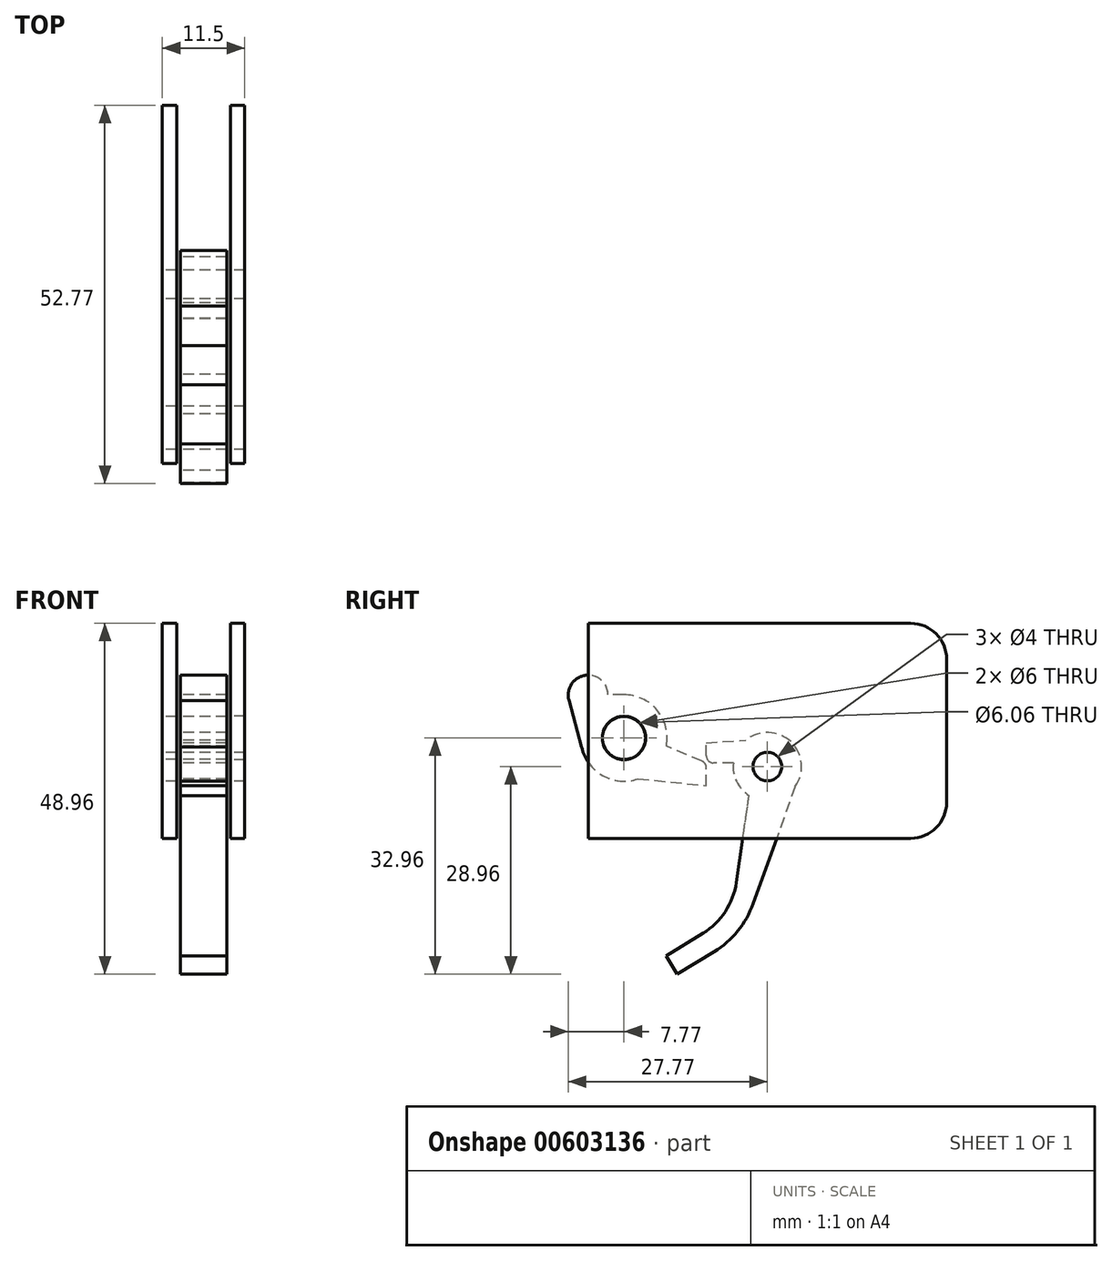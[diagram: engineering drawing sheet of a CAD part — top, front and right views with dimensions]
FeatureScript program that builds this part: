
annotation { "Feature Type Name" : "Feature", "Feature Type Description" : "" }
export const myFeature = defineFeature(function(context is Context, id is Id, definition is map)
    precondition{}
    {
        {
            var Q0;
            Q0=qCreatedBy(makeId("Right.planeOp"),FACE);
            var sketch = newSketch(context, id + "F0", { "sketchPlane" : qUnion([Q0])});
            skLineSegment(sketch, "E0.bottom", {"start": v(-20, 10) * mm, "end": v(25, 10) * mm});
            skLineSegment(sketch, "E0.top", {"start": v(-20, -20) * mm, "end": v(25, -20) * mm});
            skLineSegment(sketch, "E0.left", {"start": v(-20, 10) * mm, "end": v(-20, -20) * mm});
            skLineSegment(sketch, "E0.right", {"start": v(30, 5) * mm, "end": v(30, -15) * mm});
            skCircle(sketch, "E1", {"center": v(-15, -6) * mm, "radius": 3 * mm});
            skCircle(sketch, "E2", {"center": v(5, -10) * mm, "radius": 2 * mm});
            skPoint(sketch, "E3.visualSharp", {"position": v(30, 10) * mm});
            skArc(sketch, "E3.filletArc", {"start": v(30, 5) * mm, "mid": v(28.54, 8.54) * mm, "end": v(25, 10) * mm});
            skPoint(sketch, "E4.visualSharp", {"position": v(30, -20) * mm});
            skArc(sketch, "E4.filletArc", {"start": v(25, -20) * mm, "mid": v(28.54, -18.54) * mm, "end": v(30, -15) * mm});
            skSolve(sketch);
        }
        {
            var Q0;
            Q0 = qSketchRegion(id + "F0", true);
            extrude(context, id + "F1", {"entities" : qUnion([Q0]), "depth" : 2 * mm, "offsetDistance" : 25 * mm});
        }
        {
            var Q0;
            Q0=makeQuery(id+"F1.opExtrude","CAP_FACE",FACE,{"disambiguationData":[OSD([sQuery(id+"F0.wireOp",EDGE,"E0.bottom"),sQuery(id+"F0.wireOp",EDGE,"E0.top"),sQuery(id+"F0.wireOp",EDGE,"E0.left"),sQuery(id+"F0.wireOp",EDGE,"E0.right"),sQuery(id+"F0.wireOp",EDGE,"E1"),sQuery(id+"F0.wireOp",EDGE,"E2"),sQuery(id+"F0.wireOp",EDGE,"E3.filletArc"),sQuery(id+"F0.wireOp",EDGE,"E4.filletArc")])],"isStart":false});
            var sketch = newSketch(context, id + "F2", { "sketchPlane" : qUnion([Q0])});
            skArc(sketch, "E5", {"start": v(-20.9, -7.27) * mm, "mid": v(-17.96, -11.26) * mm, "end": v(-13.03, -11.7) * mm});
            skArc(sketch, "E6", {"start": v(0.25, -9.5) * mm, "mid": v(0.7, -12.08) * mm, "end": v(2.45, -14.04) * mm});
            skArc(sketch, "E7", {"start": v(-17.23, 0.03) * mm, "mid": v(-20.4, 2.74) * mm, "end": v(-22.66, -0.76) * mm});
            skLineSegment(sketch, "E8", {"start": v(-13.03, -11.7) * mm, "end": v(-3.5, -12.66) * mm});
            skLineSegment(sketch, "E9", {"start": v(-3.5, -12.66) * mm, "end": v(-3.5, -10.16) * mm});
            skLineSegment(sketch, "E10", {"start": v(-4.12, -9.24) * mm, "end": v(-9.07, -7.12) * mm});
            skLineSegment(sketch, "E11", {"start": v(0.25, -9.5) * mm, "end": v(-2.5, -9.5) * mm});
            skLineSegment(sketch, "E12", {"start": v(-3.5, -8.5) * mm, "end": v(-3.5, -6.69) * mm});
            skLineSegment(sketch, "E13", {"start": v(-3.5, -6.69) * mm, "end": v(2, -6.28) * mm});
            skPoint(sketch, "E14.visualSharp", {"position": v(-3.5, -9.5) * mm});
            skArc(sketch, "E14.filletArc", {"start": v(-3.5, -8.5) * mm, "mid": v(-3.22, -9.2) * mm, "end": v(-2.5, -9.5) * mm});
            skArc(sketch, "E15.filletArc", {"start": v(-3.5, -10.16) * mm, "mid": v(-3.67, -9.6) * mm, "end": v(-4.12, -9.24) * mm});
            skLineSegment(sketch, "E16", {"start": v(-14.94, 0.03) * mm, "end": v(-17.23, 0.03) * mm});
            skLineSegment(sketch, "E17", {"start": v(8.87, -12.8) * mm, "end": v(3.02, -29.12) * mm});
            skLineSegment(sketch, "E18", {"start": v(-2.42, -35.81) * mm, "end": v(-7.56, -38.96) * mm});
            skLineSegment(sketch, "E19", {"start": v(-7.56, -38.96) * mm, "end": v(-9.13, -36.4) * mm});
            skLineSegment(sketch, "E20", {"start": v(-9.13, -36.4) * mm, "end": v(-3.99, -33.25) * mm});
            skLineSegment(sketch, "E21", {"start": v(0.68, -26.18) * mm, "end": v(2.45, -14.04) * mm});
            skPoint(sketch, "E22.visualSharp", {"position": v(0, -30.8) * mm});
            skArc(sketch, "E22.filletArc", {"start": v(-3.99, -33.25) * mm, "mid": v(-0.87, -30.24) * mm, "end": v(0.68, -26.18) * mm});
            skPoint(sketch, "E23.visualSharp", {"position": v(1.48, -33.42) * mm});
            skArc(sketch, "E23.filletArc", {"start": v(-2.42, -35.81) * mm, "mid": v(0.87, -32.93) * mm, "end": v(3.02, -29.12) * mm});
            skLineSegment(sketch, "E24", {"start": v(-22.66, -0.76) * mm, "end": v(-20.9, -7.27) * mm});
            skArc(sketch, "E25.trimOffspring", {"start": v(-9.07, -7.12) * mm, "mid": v(-10.37, -2.13) * mm, "end": v(-15.06, 0.03) * mm});
            skArc(sketch, "E26.trimOffspring", {"start": v(8.87, -12.8) * mm, "mid": v(8.29, -6.54) * mm, "end": v(2, -6.28) * mm});
            skCircle(sketch, "E27", {"center": v(-15, -6) * mm, "radius": 3 * mm});
            skCircle(sketch, "E28", {"center": v(5, -10) * mm, "radius": 2 * mm});
            skSolve(sketch);
        }
        {
            var Q0;
            Q0 = qSketchRegion(id + "F2", true);
            extrude(context, id + "F3", {"entities" : qUnion([Q0]), "depth" : 7 * mm, "offsetDistance" : 25 * mm, "hasSecondDirection" : true, "secondDirectionOppositeDirection" : true, "secondDirectionDepth" : -0.5 * mm});
        }
        {
            var Q0;
            Q0=makeQuery(id+"F3.opExtrude","CAP_FACE",FACE,{"disambiguationData":[OSD([sQuery(id+"F2.wireOp",EDGE,"E5"),sQuery(id+"F2.wireOp",EDGE,"E7"),sQuery(id+"F2.wireOp",EDGE,"E8"),sQuery(id+"F2.wireOp",EDGE,"E9"),sQuery(id+"F2.wireOp",EDGE,"E10"),sQuery(id+"F2.wireOp",EDGE,"E15.filletArc"),sQuery(id+"F2.wireOp",EDGE,"E16"),sQuery(id+"F2.wireOp",EDGE,"E24"),sQuery(id+"F2.wireOp",EDGE,"E25.trimOffspring"),sQuery(id+"F2.wireOp",EDGE,"E27")])],"isStart":false});
            var sketch = newSketch(context, id + "F4", { "sketchPlane" : qUnion([Q0])});
            skLineSegment(sketch, "E29.bottom", {"start": v(-20, 10) * mm, "end": v(25, 10) * mm});
            skLineSegment(sketch, "E29.top", {"start": v(-20, -20) * mm, "end": v(25, -20) * mm});
            skLineSegment(sketch, "E29.left", {"start": v(-20, 10) * mm, "end": v(-20, -20) * mm});
            skLineSegment(sketch, "E29.right", {"start": v(30, 5) * mm, "end": v(30, -15) * mm});
            skPoint(sketch, "E30.visualSharp", {"position": v(30, 10) * mm});
            skArc(sketch, "E30.filletArc", {"start": v(30, 5) * mm, "mid": v(28.54, 8.54) * mm, "end": v(25, 10) * mm});
            skPoint(sketch, "E31.visualSharp", {"position": v(30, -20) * mm});
            skArc(sketch, "E31.filletArc", {"start": v(25, -20) * mm, "mid": v(28.54, -18.54) * mm, "end": v(30, -15) * mm});
            skCircle(sketch, "E32", {"center": v(5, -10) * mm, "radius": 2 * mm});
            skCircle(sketch, "E33", {"center": v(-15, -6) * mm, "radius": 3.03 * mm});
            skSolve(sketch);
        }
        {
            var Q0;
            Q0 = qSketchRegion(id + "F4", true);
            extrude(context, id + "F5", {"entities" : qUnion([Q0]), "depth" : 2.5 * mm, "offsetDistance" : 25 * mm, "hasSecondDirection" : true, "secondDirectionOppositeDirection" : true, "secondDirectionDepth" : -0.5 * mm});
        }
    });
